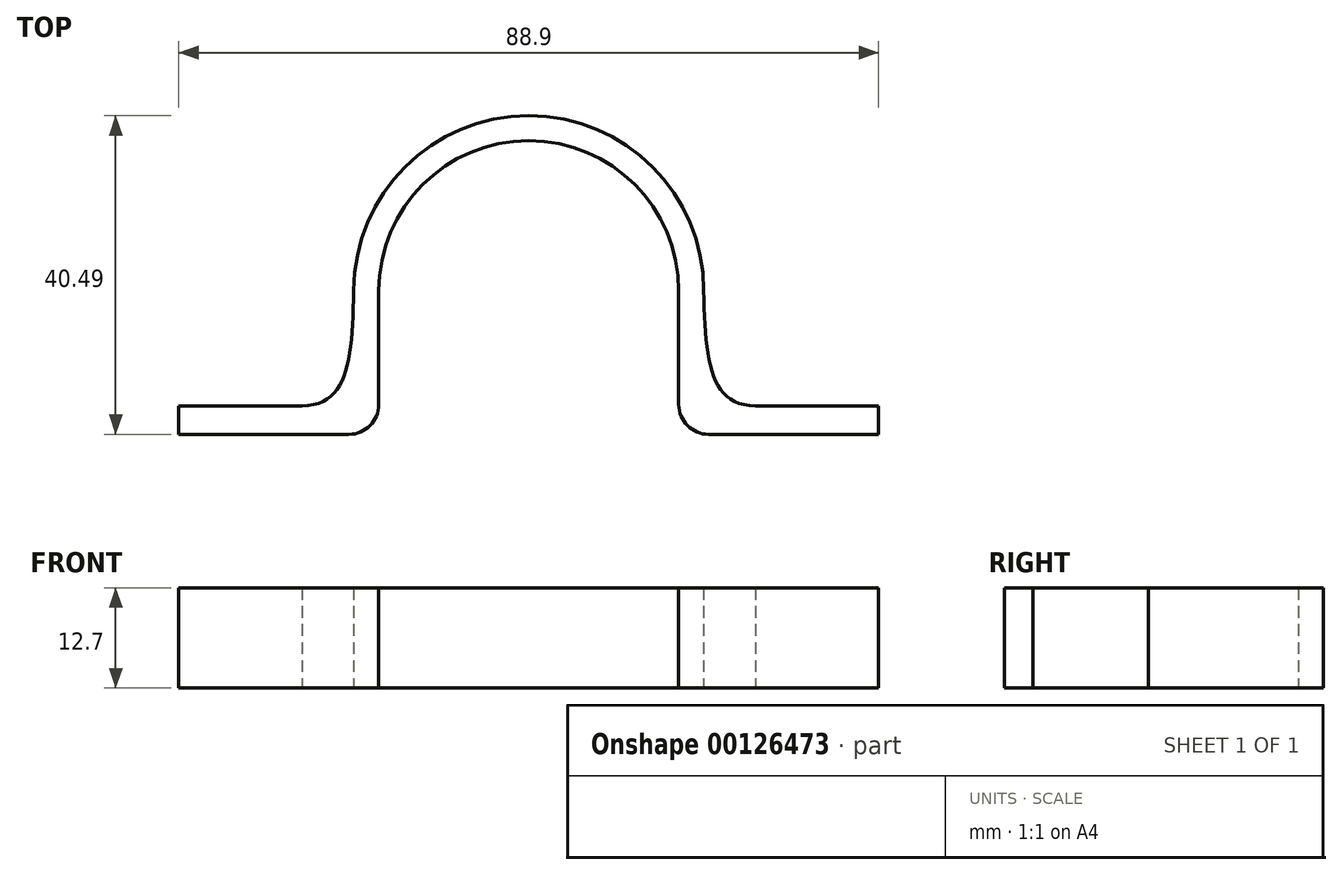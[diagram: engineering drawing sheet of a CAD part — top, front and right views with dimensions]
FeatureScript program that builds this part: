
annotation { "Feature Type Name" : "Feature", "Feature Type Description" : "" }
export const myFeature = defineFeature(function(context is Context, id is Id, definition is map)
    precondition{}
    {
        {
            var Q0;
            Q0=qCreatedBy(makeId("Top.planeOp"),FACE);
            var sketch = newSketch(context, id + "F0", { "sketchPlane" : qUnion([Q0])});
            skCircle(sketch, "E0", {"center": v(0, 0) * mm, "radius": 18.26 * mm, "construction": true});
            skCircle(sketch, "E1", {"center": v(0, 0) * mm, "radius": 19.05 * mm, "construction": true});
            skArc(sketch, "E2", {"start": v(19.05, 0) * mm, "mid": v(13.47, 13.47) * mm, "end": v(0, 19.05) * mm});
            skPoint(sketch, "E3", {"position": v(0, -18.26) * mm});
            skLineSegment(sketch, "E4", {"start": v(19.05, 0) * mm, "end": v(19.05, -14.45) * mm});
            skPoint(sketch, "E5", {"position": v(0, 19.05) * mm});
            skPoint(sketch, "E6", {"position": v(19.05, -18.26) * mm});
            skCircle(sketch, "E7", {"center": v(0, 0) * mm, "radius": 22.22 * mm, "construction": true});
            skLineSegment(sketch, "E8", {"start": v(22.86, -18.26) * mm, "end": v(44.45, -18.26) * mm});
            skArc(sketch, "E9.filletArc", {"start": v(19.05, -14.45) * mm, "mid": v(20.17, -17.14) * mm, "end": v(22.86, -18.26) * mm});
            skPoint(sketch, "E10", {"position": v(0, 22.22) * mm});
            skArc(sketch, "E11", {"start": v(22.22, 0) * mm, "mid": v(15.72, 15.72) * mm, "end": v(0, 22.22) * mm});
            skLineSegment(sketch, "E12", {"start": v(28.77, -14.68) * mm, "end": v(44.45, -14.68) * mm});
            skLineSegment(sketch, "E13", {"start": v(44.45, -14.68) * mm, "end": v(44.45, -18.26) * mm});
            skLineSegment(sketch, "E14", {"start": v(0, 0) * mm, "end": v(0, 22.22) * mm, "construction": true});
            skArc(sketch, "E15.MirrorCS", {"start": v(-22.22, 0) * mm, "mid": v(-15.72, 15.72) * mm, "end": v(0, 22.22) * mm});
            skArc(sketch, "E16.MirrorCS", {"start": v(-19.05, 0) * mm, "mid": v(-13.47, 13.47) * mm, "end": v(0, 19.05) * mm});
            skLineSegment(sketch, "E17.MirrorCS", {"start": v(-19.05, 0) * mm, "end": v(-19.05, -14.45) * mm});
            skLineSegment(sketch, "E18.MirrorCS", {"start": v(-28.77, -14.68) * mm, "end": v(-44.45, -14.68) * mm});
            skLineSegment(sketch, "E19.MirrorCS", {"start": v(-44.45, -14.68) * mm, "end": v(-44.45, -18.26) * mm});
            skLineSegment(sketch, "E20.MirrorCS", {"start": v(-22.86, -18.26) * mm, "end": v(-44.45, -18.26) * mm});
            skArc(sketch, "E21.MirrorCS", {"start": v(-19.05, -14.45) * mm, "mid": v(-20.17, -17.14) * mm, "end": v(-22.86, -18.26) * mm});
            skLineSegment(sketch, "E22", {"start": v(-22.22, 0) * mm, "end": v(22.22, 0) * mm, "construction": true});
            skLineSegment(sketch, "E23", {"start": v(-44.45, -18.26) * mm, "end": v(44.45, -18.26) * mm, "construction": true});
            skLineSegment(sketch, "E24", {"start": v(0, 0) * mm, "end": v(0, -18.26) * mm, "construction": true});
            skFitSpline(sketch, "E25", {"points": [v(22.22, 0) * mm, v(28.77, -14.68) * mm], "startDerivative": vector(0.67, -26.3) * mm, "endDerivative": vector(17.73, -0.69) * mm});
            skFitSpline(sketch, "E26.MirrorCS", {"points": [v(-22.22, 0) * mm, v(-28.77, -14.68) * mm], "startDerivative": vector(-0.67, -26.3) * mm, "endDerivative": vector(-17.73, -0.69) * mm});
            skSolve(sketch);
        }
        {
            var Q0;
            Q0 = qSketchRegion(id + "F0", true);
            extrude(context, id + "F1", {"entities" : qUnion([Q0]), "depth" : 12.7 * mm});
        }
    });
